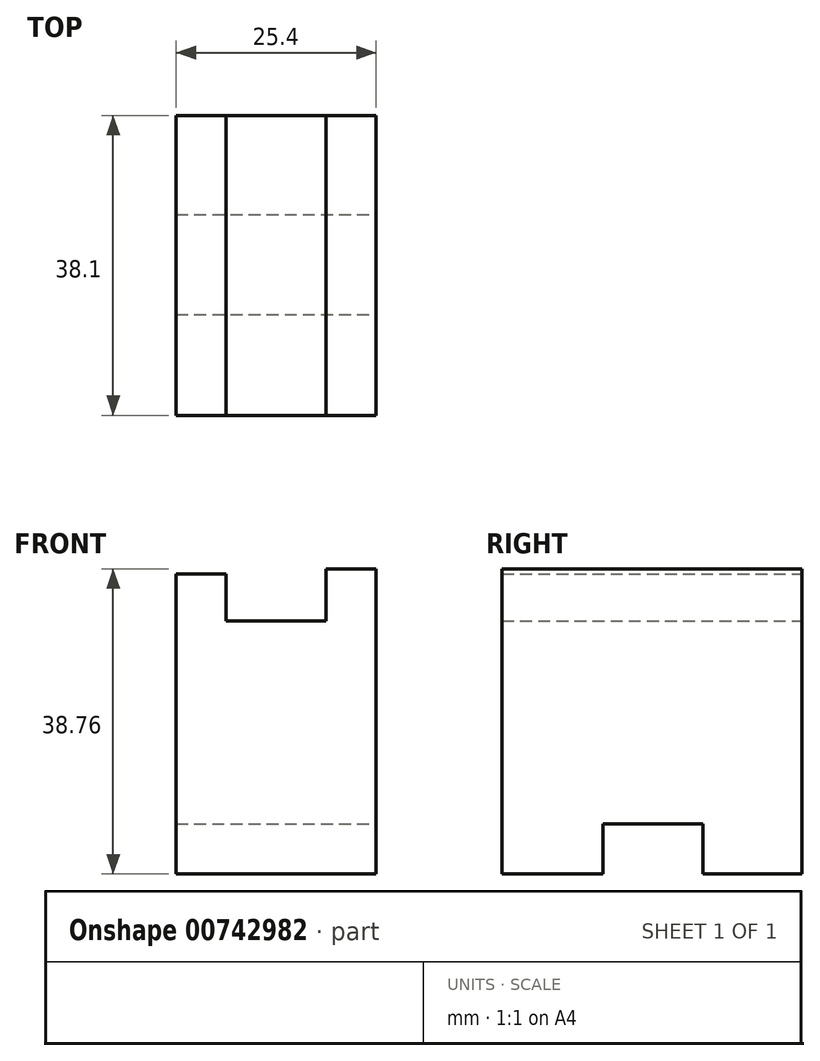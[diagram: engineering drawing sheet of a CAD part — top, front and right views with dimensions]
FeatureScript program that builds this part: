
annotation { "Feature Type Name" : "Feature", "Feature Type Description" : "" }
export const myFeature = defineFeature(function(context is Context, id is Id, definition is map)
    precondition{}
    {
        {
            var Q0;
            Q0=qCreatedBy(makeId("Front.planeOp"),FACE);
            var sketch = newSketch(context, id + "F0", { "sketchPlane" : qUnion([Q0])});
            skLineSegment(sketch, "E0", {"start": v(0, 0) * mm, "end": v(0, 38.1) * mm});
            skLineSegment(sketch, "E1", {"start": v(0, 38.1) * mm, "end": v(6.35, 38.1) * mm});
            skLineSegment(sketch, "E2", {"start": v(6.35, 38.1) * mm, "end": v(6.35, 32.14) * mm});
            skLineSegment(sketch, "E3", {"start": v(6.35, 32.14) * mm, "end": v(19.05, 32.14) * mm});
            skLineSegment(sketch, "E4", {"start": v(19.05, 32.14) * mm, "end": v(19.05, 38.76) * mm});
            skLineSegment(sketch, "E5", {"start": v(19.05, 38.76) * mm, "end": v(25.4, 38.76) * mm});
            skLineSegment(sketch, "E6", {"start": v(25.4, 38.76) * mm, "end": v(25.4, 0) * mm});
            skLineSegment(sketch, "E7", {"start": v(25.4, 0) * mm, "end": v(0, 0) * mm});
            skSolve(sketch);
        }
        {
            var Q0;
            Q0=makeQuery(id+"F0.imprint","IMPRINT",FACE,{"disambiguationData":[TD([[makeQuery(id+"F0.imprint","IMPRINT",EDGE,{"derivedFrom":sQuery(id+"F0.wireOp",EDGE,"E0")}),-1.0]])]});
            extrude(context, id + "F1", {"entities" : qUnion([Q0]), "depth" : 38.1 * mm, "offsetDistance" : 25.4 * mm});
        }
        {
            var Q0;
            Q0=makeQuery(id+"F1.opExtrude","SWEPT_FACE",FACE,{"disambiguationData":[OSD([sQuery(id+"F0.wireOp",EDGE,"E6")])]});
            var sketch = newSketch(context, id + "F2", { "sketchPlane" : qUnion([Q0])});
            skLineSegment(sketch, "E8", {"start": v(-25.27, 0) * mm, "end": v(-25.27, 6.35) * mm});
            skLineSegment(sketch, "E9", {"start": v(-25.27, 6.35) * mm, "end": v(-12.57, 6.35) * mm});
            skLineSegment(sketch, "E10", {"start": v(-12.57, 6.35) * mm, "end": v(-12.57, 0) * mm});
            skSolve(sketch);
        }
        {
            var Q0;
            Q0 = qSketchRegion(id + "F2", true);
            var Q1;
            {var subQ0=sQuery(id+"F2.wireOp",EDGE,"E8");Q1=makeQuery(id+"F2.imprint","IMPRINT",FACE,{"disambiguationData":[TD([[makeQuery(id+"F2.imprint","IMPRINT",EDGE,{"derivedFrom":subQ0}),-1.0]])]});}
            extrude(context, id + "F3", {"entities" : qUnion([Q0, Q1]), "operationType" : NewBodyOperationType.REMOVE, "oppositeDirection" : true, "depth" : 25.4 * mm, "offsetDistance" : 25.4 * mm});
        }
    });
